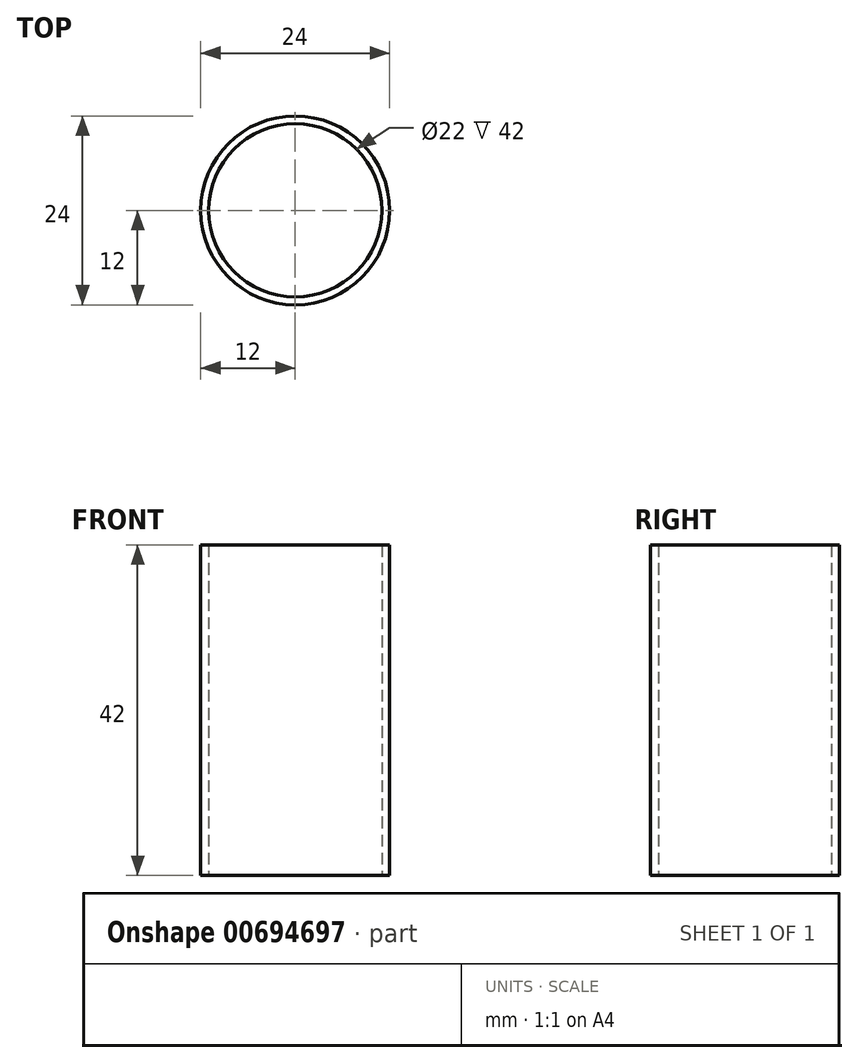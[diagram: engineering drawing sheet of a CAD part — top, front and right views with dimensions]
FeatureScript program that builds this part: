
annotation { "Feature Type Name" : "Feature", "Feature Type Description" : "" }
export const myFeature = defineFeature(function(context is Context, id is Id, definition is map)
    precondition{}
    {
        {
            var Q0;
            Q0=qCreatedBy(makeId("Top.planeOp"),FACE);
            var sketch = newSketch(context, id + "F0", { "sketchPlane" : qUnion([Q0])});
            skCircle(sketch, "E0", {"center": v(0, 0) * mm, "radius": 12 * mm});
            skCircle(sketch, "E1", {"center": v(0, 0) * mm, "radius": 11 * mm});
            skSolve(sketch);
        }
        {
            var Q0;
            Q0=makeQuery(id+"F0.imprint","IMPRINT",FACE,{"disambiguationData":[TD([[makeQuery(id+"F0.imprint","IMPRINT",EDGE,{"derivedFrom":sQuery(id+"F0.wireOp",EDGE,"E0")}),1.0]])]});
            extrude(context, id + "F1", {"entities" : qUnion([Q0]), "depth" : 42 * mm, "offsetDistance" : 25 * mm});
        }
    });
